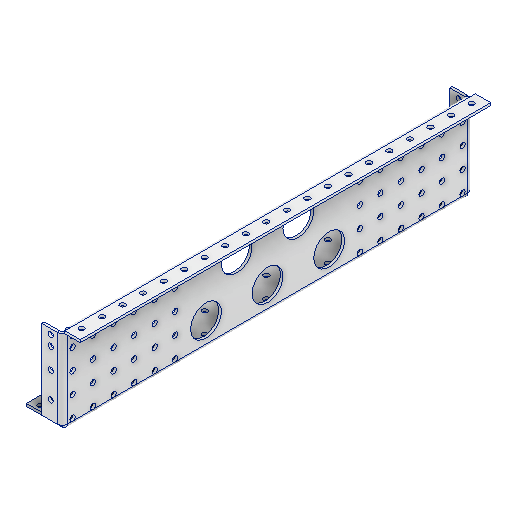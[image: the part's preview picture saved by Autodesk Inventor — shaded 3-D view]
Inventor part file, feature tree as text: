
AUTODESK INVENTOR PART (.ipt)
format: ipt  version: 2022 (Build 260153000, 153)  size: 691,200 bytes
history: native  units: in
note: dims shown in document units (in); Inventor stores cm internally (conversion verified against a paired STEP export)
features: other x12, sketch x11, sheet_metal_op x10, pattern_linear x4
ambient origin geometry x8: Origin, YZ Plane, XZ Plane, XY Plane, X Axis, Y Axis, Z Axis, Center Point
bodies: Solid1 (feature_tree)
feature tree (37):
  sheet_metal_op  "Face1"
  sheet_metal_op  "Flange1"
  sheet_metal_op  "Flange2"
  pattern_linear  "Rectangular Pattern1"  Spacing1=0.125in  [1 undecoded]
  pattern_linear  "Rectangular Pattern2"  Spacing1=0.0625in  [1 undecoded]
  pattern_linear  "Rectangular Pattern3"  Spacing1=0.25in  [1 undecoded]
  sheet_metal_op  "Flange3"
  pattern_linear  "Rectangular Pattern6"  Spacing1=0.125in  [1 undecoded]
  sketch  "Sketch1"  dims[d0=4.375in]
  other  "Plate1"
  sketch  "Sketch2"  dims[d1=20.0in]
  other  "Plate2"
  sheet_metal_op  "Bend1"
  sheet_metal_op  "Corner1"
  sketch  "Sketch3"  dims[d2=0.125in]
  other  "Plate3"
  sheet_metal_op  "Bend2"
  sheet_metal_op  "Corner2"
  sketch  "Sketch4"  dims[d3=0.125in]
  sketch  "Sketch5"  dims[d4=0.0625in]
  sketch  "Sketch6"  dims[d5=0.25in]
  sketch  "Sketch7"  dims[d6=0.125in]
  sketch  "Sketch8"  dims[d7=1.0in d8=90.0deg d9=0.125in]
  other  "Plate4"
  sheet_metal_op  "Bend3"
  sheet_metal_op  "Corner3"
  sketch  "Sketch11"  dims[d10=0.5in]
  sketch  "Sketch12"  dims[d11=0.125in]
  sketch  "Sketch13"  dims[d12=0.125in d13=0.125in d14=0.0625in d15=0.25in d16=0.125in d17=2.0in d18=90.0deg d19=0.125in d20=0.5in d21=0.125in d22=0.125in d23=1.5in d24=1.5in d25=1.25in d26=3.25in d27=1.5in d28=3.25in d29=10.0in d30=1.5in d31=1.5in d32=1.5in d33=3.0in d34=1.25in d35=1.5in d36=3.0in d37=1.25in d38=0.125in d39=0.0in d41=0.5in d42=0.44in d43=0.125in d44=0.0in d45=7.874in d47=1.0in d48=0.26in d50=0.5in d51=0.125in d52=0.0in d53=7.874in d55=1.0in d56=0.435in d57=0.26in d58=0.26in d59=0.26in d60=0.26in d61=1.0in d62=1.0in d63=1.0in d64=0.375in d65=0.5in d66=0.26in d67=0.5in d68=0.5in d69=0.26in d70=0.375in d71=0.5in d72=0.26in d73=0.26in d74=1.0in d75=1.0in d76=0.26in d77=1.0in d78=0.26in d79=0.5in d80=0.5in d81=0.125in d82=0.0in d83=2.3622in d85=1.0in d86=2.3622in d88=1.0in d89=0.125in d90=0.0625in d91=0.25in d92=0.125in d93=1.0in d94=90.0deg d95=0.125in d96=0.5in d97=0.125in d98=0.125in d115=0.26in d116=0.44in d118=0.26in d119=1.25in d120=0.26in d121=2.25in d122=0.26in d124=0.875in d125=0.5in d126=0.125in d127=0.0in d128=0.26in d129=0.875in d130=0.44in d131=0.26in d132=1.25in d133=0.26in d134=1.0in d135=0.26in d136=0.44in d137=0.5in d138=0.125in d139=0.0in d140=0.125in d141=0.0in d142=0.7874in d144=1.0in]
  other  "Cut1"
  other  "Cut2"
  other  "Cut3"
  other  "Cut4"
  other  "Cut7"
  other  "Cut8"
  other  "Cut9"
  other  "Definition1"
note: 4 required parameter values undecoded (feature->parameter linkage not recoverable at this tier; creation-order binding heuristic only, values carry confidence <= 0.55)
